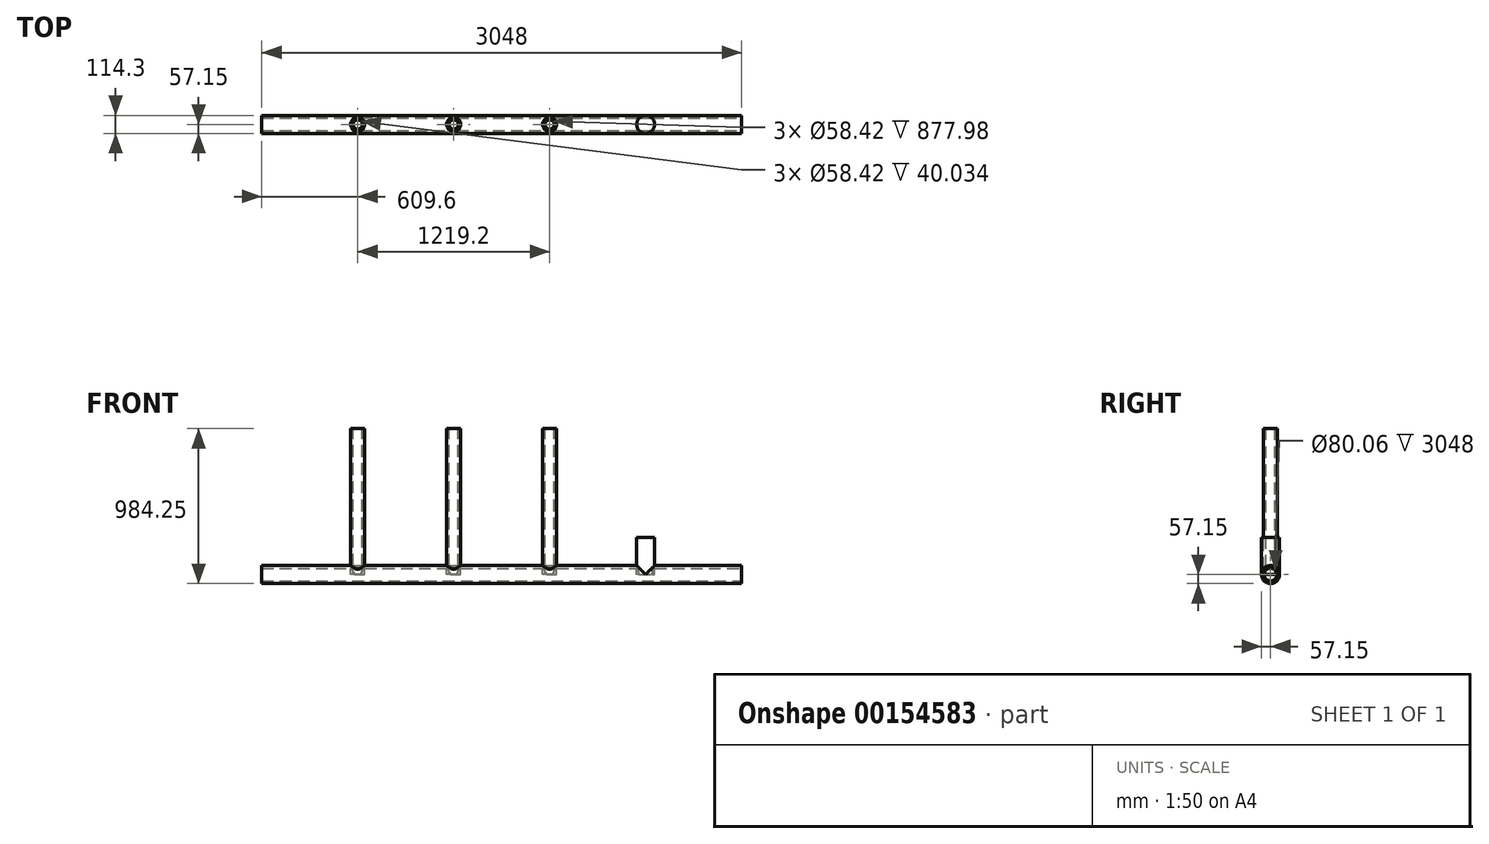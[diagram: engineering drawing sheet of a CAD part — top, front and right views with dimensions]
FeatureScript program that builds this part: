
annotation { "Feature Type Name" : "Feature", "Feature Type Description" : "" }
export const myFeature = defineFeature(function(context is Context, id is Id, definition is map)
    precondition{}
    {
        {
            var Q0;
            Q0=qCreatedBy(makeId("Front.planeOp"),FACE);
            var sketch = newSketch(context, id + "F0", { "sketchPlane" : qUnion([Q0])});
            skLineSegment(sketch, "E0", {"start": v(0, 0) * mm, "end": v(3048, 0) * mm});
            skLineSegment(sketch, "E1", {"start": v(609.6, 927.1) * mm, "end": v(609.6, 0) * mm});
            skLineSegment(sketch, "E2", {"start": v(1219.2, 927.1) * mm, "end": v(1219.2, 0) * mm});
            skLineSegment(sketch, "E3", {"start": v(1828.8, 927.1) * mm, "end": v(1828.8, 0) * mm});
            skLineSegment(sketch, "E4", {"start": v(2438.4, 236.6) * mm, "end": v(2438.4, 0) * mm});
            skPoint(sketch, "E5", {"position": v(609.6, 0) * mm});
            skPoint(sketch, "E6", {"position": v(1219.2, 0) * mm});
            skPoint(sketch, "E7", {"position": v(1828.8, 0) * mm});
            skPoint(sketch, "E8", {"position": v(2438.4, 0) * mm});
            skSolve(sketch);
        }
        {
            var Q0;
            Q0=qCreatedBy(makeId("Right.planeOp"),FACE);
            var sketch = newSketch(context, id + "F1", { "sketchPlane" : qUnion([Q0])});
            skCircle(sketch, "E9", {"center": v(0, 0) * mm, "radius": 57.15 * mm});
            skCircle(sketch, "E10.0", {"center": v(0, 0) * mm, "radius": 40.03 * mm});
            skSolve(sketch);
        }
        {
            var Q0;
            Q0=makeQuery(id+"F1.imprint","IMPRINT",FACE,{"disambiguationData":[TD([[makeQuery(id+"F1.imprint","IMPRINT",EDGE,{"derivedFrom":sQuery(id+"F1.wireOp",EDGE,"E9")}),1.0]])]});
            var Q1;
            Q1=sQuery(id+"F0.wireOp",EDGE,"E0");
            sweep(context, id + "F2", {"profiles" : qUnion([Q0]), "path" : qUnion([Q1])});
        }
        {
            var Q0;
            Q0=qCreatedBy(makeId("Top.planeOp"),FACE);
            var sketch = newSketch(context, id + "F3", { "sketchPlane" : qUnion([Q0])});
            skCircle(sketch, "E11", {"center": v(609.6, 0) * mm, "radius": 44.45 * mm});
            skCircle(sketch, "E12", {"center": v(1219.2, 0) * mm, "radius": 44.45 * mm});
            skCircle(sketch, "E13", {"center": v(1828.8, 0) * mm, "radius": 44.45 * mm});
            skCircle(sketch, "E14", {"center": v(2438.4, 0) * mm, "radius": 57.15 * mm});
            skCircle(sketch, "E15.0", {"center": v(609.6, 0) * mm, "radius": 29.21 * mm});
            skCircle(sketch, "E16.0", {"center": v(1219.2, 0) * mm, "radius": 29.21 * mm});
            skCircle(sketch, "E17.0", {"center": v(1828.8, 0) * mm, "radius": 29.21 * mm});
            skSolve(sketch);
        }
        {
            var Q0;
            Q0=makeQuery(id+"F3.imprint","IMPRINT",FACE,{"disambiguationData":[TD([[makeQuery(id+"F3.imprint","IMPRINT",EDGE,{"derivedFrom":sQuery(id+"F3.wireOp",EDGE,"E11")}),1.0]])]});
            var Q1;
            Q1=makeQuery(id+"F3.imprint","IMPRINT",FACE,{"disambiguationData":[TD([[makeQuery(id+"F3.imprint","IMPRINT",EDGE,{"derivedFrom":sQuery(id+"F3.wireOp",EDGE,"E12")}),1.0]])]});
            var Q2;
            Q2=makeQuery(id+"F3.imprint","IMPRINT",FACE,{"disambiguationData":[TD([[makeQuery(id+"F3.imprint","IMPRINT",EDGE,{"derivedFrom":sQuery(id+"F3.wireOp",EDGE,"E13")}),1.0]])]});
            var Q3;
            Q3=sQuery(id+"F0.wireOp",EDGE,"E1");
            sweep(context, id + "F4", {"operationType" : NewBodyOperationType.ADD, "profiles" : qUnion([Q0, Q1, Q2]), "path" : qUnion([Q3])});
        }
        {
            var Q0;
            Q0=makeQuery(id+"F3.imprint","IMPRINT",FACE,{"disambiguationData":[TD([[makeQuery(id+"F3.imprint","IMPRINT",EDGE,{"derivedFrom":sQuery(id+"F3.wireOp",EDGE,"E14")}),1.0]])]});
            var Q1;
            Q1=sQuery(id+"F0.wireOp",EDGE,"E4");
            sweep(context, id + "F5", {"operationType" : NewBodyOperationType.ADD, "profiles" : qUnion([Q0]), "path" : qUnion([Q1])});
        }
    });
